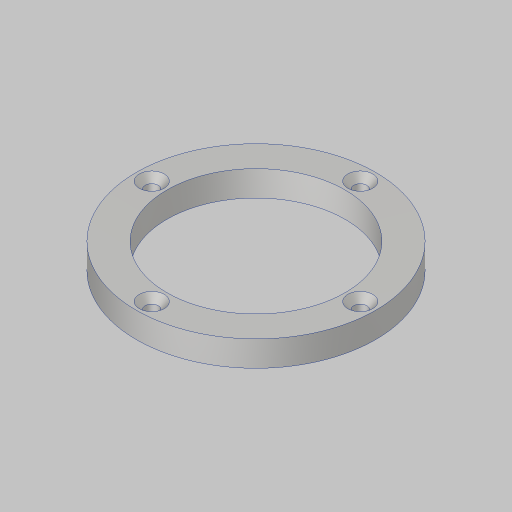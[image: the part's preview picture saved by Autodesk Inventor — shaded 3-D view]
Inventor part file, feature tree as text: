
AUTODESK INVENTOR PART (.ipt)
format: ipt  version: 2023.5 (Build 275446000, 446)  size: 201,216 bytes
history: native  units: in
note: dims shown in document units (in); Inventor stores cm internally (conversion verified against a paired STEP export)
features: sketch x2, extrude x1, hole x1, projected_geometry x1
ambient origin geometry x8: Origin, YZ Plane, XZ Plane, XY Plane, X Axis, Y Axis, Z Axis, Center Point
bodies: Solid1 (feature_tree)
feature tree (5):
  extrude  "Extrusion1"  Depth=4.7244in
  hole  "Hole1"  [1 undecoded]
  sketch  "Sketch1"  dims[d0=2.7559in d1=4.7244in]
  sketch  "Sketch2"  dims[d2=0.3937in d3=0.0in d4=0.4724in d5=0.201in d6=0.75in d7=0.385in d8=0.25in d9=0.5635in d10=1.0in d11=0.8108in d15=0.4724in d16=1.5748in d18=360.0deg]
  projected_geometry  "Project Cut Edges1"
note: 1 required parameter value undecoded (feature->parameter linkage not recoverable at this tier; creation-order binding heuristic only, values carry confidence <= 0.55)
